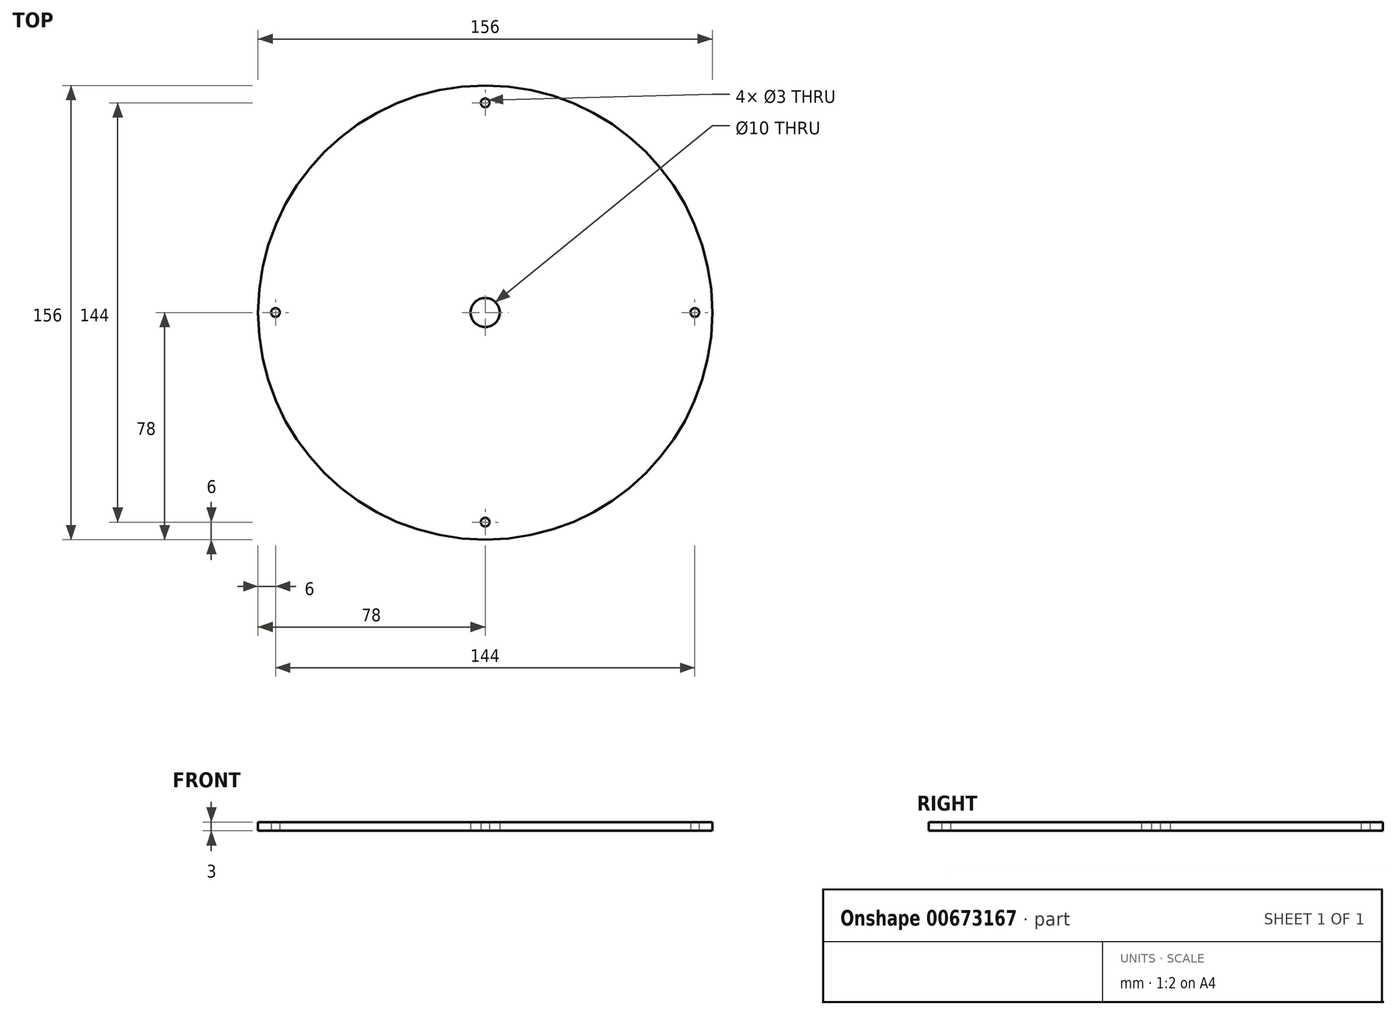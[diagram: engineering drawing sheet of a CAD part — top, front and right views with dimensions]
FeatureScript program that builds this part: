
annotation { "Feature Type Name" : "Feature", "Feature Type Description" : "" }
export const myFeature = defineFeature(function(context is Context, id is Id, definition is map)
    precondition{}
    {
        {
            var Q0;
            Q0=qCreatedBy(makeId("Top.planeOp"),FACE);
            var sketch = newSketch(context, id + "F0", { "sketchPlane" : qUnion([Q0])});
            skCircle(sketch, "E0", {"center": v(0, 0) * mm, "radius": 78 * mm});
            skCircle(sketch, "E1", {"center": v(0, 72) * mm, "radius": 1.5 * mm});
            skCircle(sketch, "E2", {"center": v(72, 0) * mm, "radius": 1.5 * mm});
            skCircle(sketch, "E3", {"center": v(0, 0) * mm, "radius": 5 * mm});
            skCircle(sketch, "E4.MirrorC", {"center": v(0, -72) * mm, "radius": 1.5 * mm});
            skCircle(sketch, "E5.MirrorC", {"center": v(-72, 0) * mm, "radius": 1.5 * mm});
            skSolve(sketch);
        }
        {
            var Q0;
            Q0=makeQuery(id+"F0.imprint","IMPRINT",FACE,{"disambiguationData":[TD([[makeQuery(id+"F0.imprint","IMPRINT",EDGE,{"derivedFrom":sQuery(id+"F0.wireOp",EDGE,"E0")}),1.0]])]});
            extrude(context, id + "F1", {"entities" : qUnion([Q0]), "depth" : 3 * mm, "offsetDistance" : 25 * mm});
        }
    });
